SOLIDWORKS PART (.sldprt)
format: sldprt  version: not decoded by parser v0  size: 316,416 bytes
history: native  units: mm
features: sketch x6, cut_extrude x4, extrude x2, material x1, plane x1 (+13 scaffold rows collapsed)
feature tree (27):
  scaffold x13  (default folders/planes/origin — collapsed)
  material  "Pine"
  sketch  "Sketch1"  dims[c1.D4=76.2mm c1.D1=25.4mm c1.D2=~650.909148mm c2.D2=~0.717899deg c3.D2=101.6mm c3.D3=127.0mm]
  extrude  "Boss-Extrude1"  Depth=12.7mm
  sketch  "Sketch2"  dims[c1.D1=0.254mm c1.D2=0.254mm c1.D3=0.254mm c2.D1=0.254mm c2.D3=0.254mm c2.D4=0.254mm c2.D5=0.254mm c2.D6=0.254mm c2.D7=0.254mm c2.D8=0.254mm c2.D9=0.254mm c2.D10=0.254mm]
  extrude  "Boss-Extrude2"  [1 undecoded]
  sketch  "Sketch3"  dims[D1=6.604mm]
  cut_extrude  "Cut-Extrude1"  [1 undecoded]
  sketch  "Sketch4"  dims[D1=12.7mm]
  cut_extrude  "Cut-Extrude2"  [1 undecoded]
  sketch  "Sketch5"  dims[D1=6.604mm]
  cut_extrude  "Cut-Extrude3"  [1 undecoded]
  plane  "Plane1"
  sketch  "Sketch7"  dims[c1.D3=3.302mm c1.D1=88.9mm c1.D2=~4.067929mm c2.D2=45.0deg c2.D3=12.7mm c2.D4=101.6mm]
  cut_extrude  "Cut-Extrude4"  [1 undecoded]
decode coverage: 7 of 12 modeling features carry decoded parameters
note: ~ marks probable driven/reference dimensions
note: 5 parameter values undecoded
summary: no parameter record found for 5 features
note: suppression state not decoded; provenance and decode notes live in map.json
